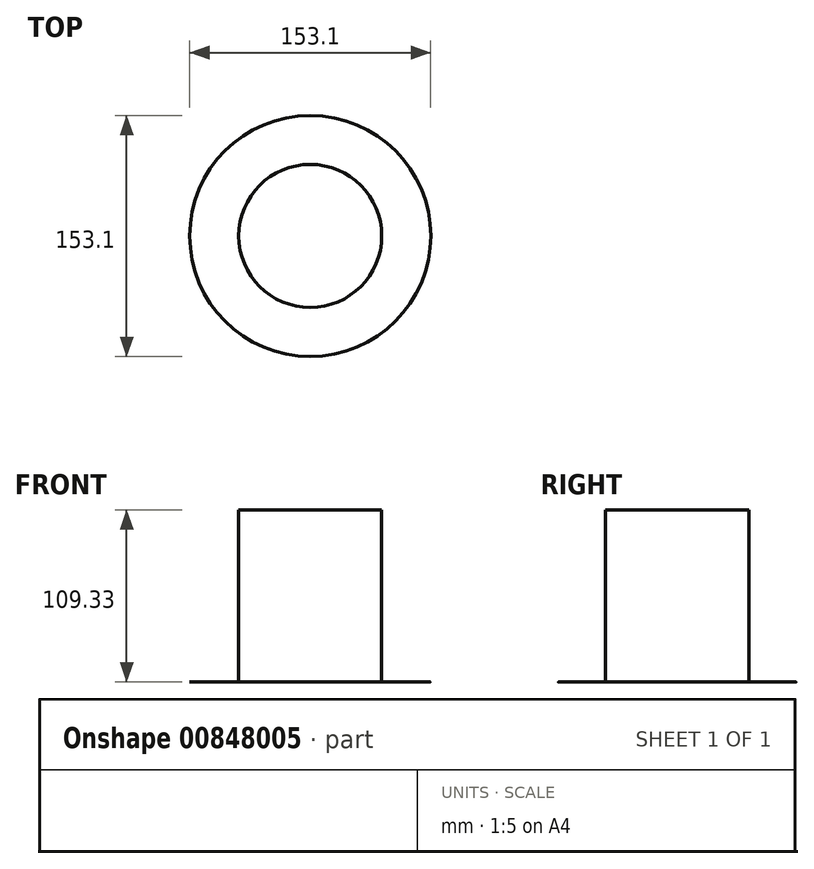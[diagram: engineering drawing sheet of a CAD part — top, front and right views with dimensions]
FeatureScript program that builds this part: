
annotation { "Feature Type Name" : "Feature", "Feature Type Description" : "" }
export const myFeature = defineFeature(function(context is Context, id is Id, definition is map)
    precondition{}
    {
        {
            var Q0;
            Q0=qCreatedBy(makeId("Front.planeOp"),FACE);
            var sketch = newSketch(context, id + "F0", { "sketchPlane" : qUnion([Q0])});
            skLineSegment(sketch, "E0", {"start": v(-76.55, -35.48) * mm, "end": v(-45.43, -35.48) * mm});
            skLineSegment(sketch, "E1", {"start": v(-45.43, -35.48) * mm, "end": v(-45.43, 73.85) * mm});
            skLineSegment(sketch, "E2", {"start": v(-45.43, 73.85) * mm, "end": v(0, 73.85) * mm});
            skLineSegment(sketch, "E3", {"start": v(0, 73.85) * mm, "end": v(0, -35.48) * mm});
            skSolve(sketch);
        }
        {
            var Q0;
            Q0=sQuery(id+"F0.wireOp",EDGE,"E2");
            var Q1;
            Q1=sQuery(id+"F0.wireOp",EDGE,"E0");
            var Q2;
            Q2=sQuery(id+"F0.wireOp",EDGE,"E1");
            var Q3;
            Q3=sQuery(id+"F0.wireOp",EDGE,"E3");
            revolve(context, id + "F1", {"bodyType" : ToolBodyType.SURFACE, "surfaceOperationType" : NewSurfaceOperationType.NEW, "surfaceEntities" : qUnion([Q0, Q1, Q2]), "axis" : qUnion([Q3]), "revolveType" : RevolveType.FULL});
        }
    });
